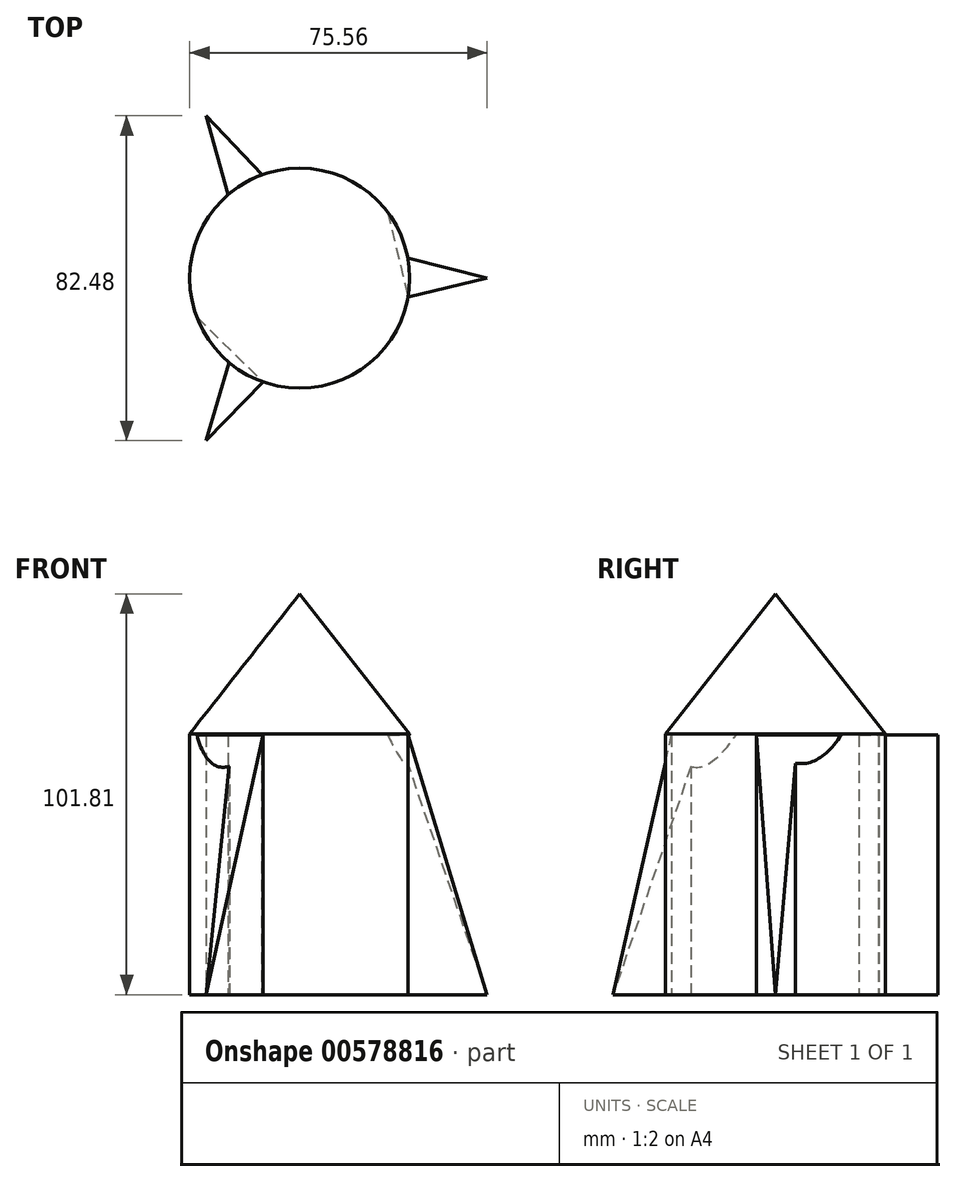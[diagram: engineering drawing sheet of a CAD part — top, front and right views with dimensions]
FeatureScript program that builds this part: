
annotation { "Feature Type Name" : "Feature", "Feature Type Description" : "" }
export const myFeature = defineFeature(function(context is Context, id is Id, definition is map)
    precondition{}
    {
        {
            var Q0;
            Q0=qCreatedBy(makeId("Right.planeOp"),FACE);
            var sketch = newSketch(context, id + "F0", { "sketchPlane" : qUnion([Q0])});
            skLineSegment(sketch, "E0", {"start": v(0, 101.81) * mm, "end": v(27.94, 66.28) * mm});
            skLineSegment(sketch, "E1", {"start": v(27.94, 66.28) * mm, "end": v(27.94, 0) * mm});
            skLineSegment(sketch, "E2", {"start": v(27.94, 0) * mm, "end": v(0, 0) * mm});
            skLineSegment(sketch, "E3", {"start": v(0, 0) * mm, "end": v(0, 101.81) * mm});
            skSolve(sketch);
        }
        {
            var Q0;
            Q0=makeQuery(id+"F0.imprint","IMPRINT",FACE,{"disambiguationData":[TD([[makeQuery(id+"F0.imprint","IMPRINT",EDGE,{"derivedFrom":sQuery(id+"F0.wireOp",EDGE,"E0")}),-1.0]])]});
            var Q1;
            Q1=sQuery(id+"F0.wireOp",EDGE,"E3");
            revolve(context, id + "F1", {"entities" : qUnion([Q0]), "axis" : qUnion([Q1]), "revolveType" : RevolveType.FULL});
        }
        {
            var Q0;
            Q0=qCreatedBy(makeId("Top.planeOp"),FACE);
            var sketch = newSketch(context, id + "F2", { "sketchPlane" : qUnion([Q0])});
            skLineSegment(sketch, "E4", {"start": v(27.17, 5.21) * mm, "end": v(47.62, 0) * mm});
            skLineSegment(sketch, "E5", {"start": v(47.62, 0) * mm, "end": v(27.53, -4.82) * mm});
            skLineSegment(sketch, "E6", {"start": v(27.17, 5.21) * mm, "end": v(27.53, -4.82) * mm});
            skLineSegment(sketch, "E7.1.0", {"start": v(-23.8, 41.24) * mm, "end": v(-9.6, 26.25) * mm});
            skLineSegment(sketch, "E7.2.0", {"start": v(-23.8, -41.24) * mm, "end": v(-17.94, -21.44) * mm});
            skPoint(sketch, "E7.center", {"position": v(0, 0) * mm});
            skLineSegment(sketch, "E8.1.1", {"start": v(-18.1, 20.93) * mm, "end": v(-23.8, 41.24) * mm});
            skLineSegment(sketch, "E8.1.2", {"start": v(-18.1, 20.93) * mm, "end": v(-9.6, 26.25) * mm});
            skLineSegment(sketch, "E8.2.1", {"start": v(-9.07, -26.14) * mm, "end": v(-23.8, -41.24) * mm});
            skLineSegment(sketch, "E8.2.2", {"start": v(-9.07, -26.14) * mm, "end": v(-17.94, -21.44) * mm});
            skSolve(sketch);
        }
        {
            var Q0;
            Q0 = qSketchRegion(id + "F2", true);
            extrude(context, id + "F3", {"entities" : qUnion([Q0]), "operationType" : NewBodyOperationType.ADD, "depth" : 66 * mm, "offsetDistance" : 25 * mm});
        }
        {
            var Q0;
            Q0=makeQuery(id+"F3.opExtrude","SWEPT_FACE",FACE,{"disambiguationData":[OSD([sQuery(id+"F2.wireOp",EDGE,"E5")])]});
            var sketch = newSketch(context, id + "F4", { "sketchPlane" : qUnion([Q0])});
            skLineSegment(sketch, "E9", {"start": v(25.65, 66) * mm, "end": v(46.3, 0) * mm});
            skLineSegment(sketch, "E10", {"start": v(46.3, 0) * mm, "end": v(46.3, 66) * mm});
            skLineSegment(sketch, "E11", {"start": v(46.3, 66) * mm, "end": v(25.65, 66) * mm});
            skSolve(sketch);
        }
        {
            var Q0;
            Q0 = qSketchRegion(id + "F4", true);
            extrude(context, id + "F5", {"entities" : qUnion([Q0]), "operationType" : NewBodyOperationType.REMOVE, "oppositeDirection" : true, "depth" : 25 * mm, "offsetDistance" : 25 * mm});
        }
        {
            var Q0;
            Q0=makeQuery(id+"F3.opExtrude","SWEPT_FACE",FACE,{"disambiguationData":[OSD([sQuery(id+"F2.wireOp",EDGE,"E8.2.1")])]});
            var sketch = newSketch(context, id + "F6", { "sketchPlane" : qUnion([Q0])});
            skLineSegment(sketch, "E12", {"start": v(-46.14, 0) * mm, "end": v(-25.34, 66) * mm});
            skLineSegment(sketch, "E13", {"start": v(-46.14, 0) * mm, "end": v(-46.14, 66) * mm});
            skLineSegment(sketch, "E14", {"start": v(-46.14, 66) * mm, "end": v(-25.34, 66) * mm});
            skSolve(sketch);
        }
        {
            var Q0;
            Q0=makeQuery(id+"F6.imprint","IMPRINT",FACE,{"disambiguationData":[TD([[makeQuery(id+"F6.imprint","IMPRINT",EDGE,{"derivedFrom":sQuery(id+"F6.wireOp",EDGE,"E12")}),1.0]])]});
            extrude(context, id + "F7", {"entities" : qUnion([Q0]), "operationType" : NewBodyOperationType.REMOVE, "oppositeDirection" : true, "depth" : 25 * mm, "offsetDistance" : 25 * mm});
        }
    });
